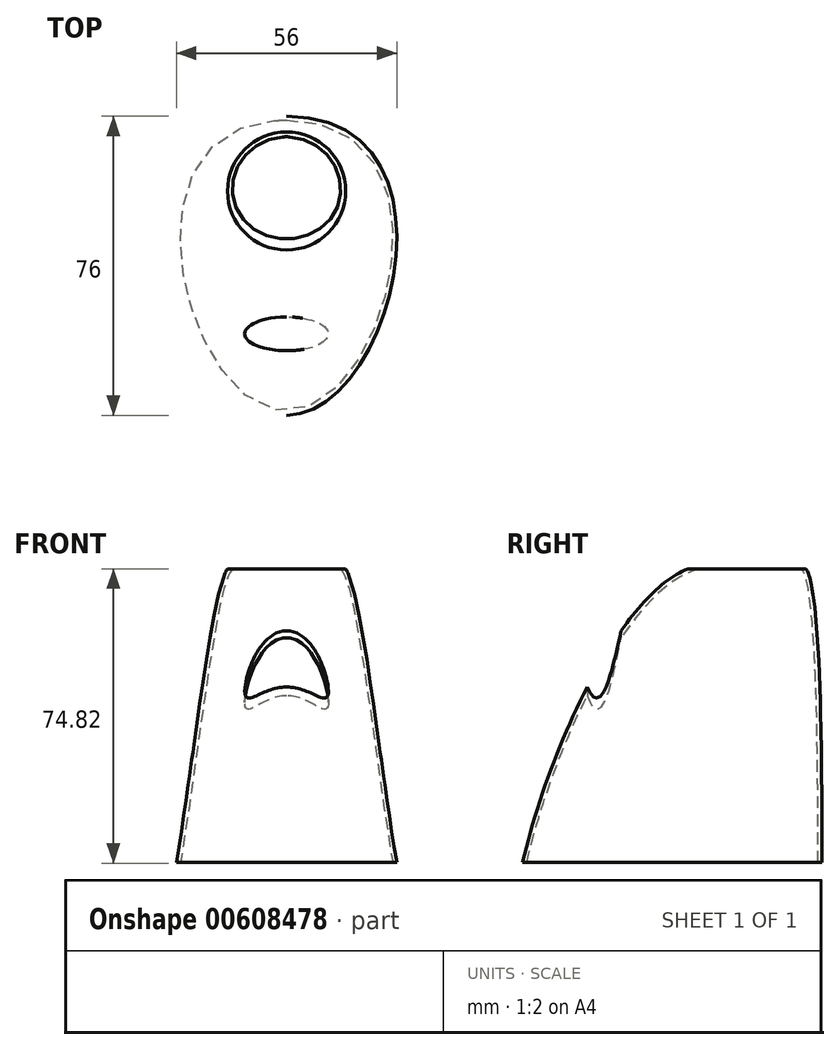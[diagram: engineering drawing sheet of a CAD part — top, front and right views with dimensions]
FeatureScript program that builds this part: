
annotation { "Feature Type Name" : "Feature", "Feature Type Description" : "" }
export const myFeature = defineFeature(function(context is Context, id is Id, definition is map)
    precondition{}
    {
        {
            var Q0;
            Q0=qCreatedBy(makeId("Top.planeOp"),FACE);
            var sketch = newSketch(context, id + "F0", { "sketchPlane" : qUnion([Q0])});
            skLineSegment(sketch, "E0", {"start": v(0, 0) * mm, "end": v(0, 38) * mm, "construction": true});
            skLineSegment(sketch, "E1", {"start": v(0, 0) * mm, "end": v(0, -38) * mm, "construction": true});
            skFitSpline(sketch, "E2", {"points": [v(0, 38) * mm, v(0, -38) * mm], "startDerivative": vector(139.24, 0) * mm, "endDerivative": vector(-81.05, 0) * mm});
            skLineSegment(sketch, "E3", {"start": v(28, 48.42) * mm, "end": v(28, -48.42) * mm, "construction": true});
            skFitSpline(sketch, "E4.MirrorCS", {"points": [v(0, 38) * mm, v(0, -38) * mm], "startDerivative": vector(-139.24, 0) * mm, "endDerivative": vector(81.05, 0) * mm});
            skSolve(sketch);
        }
        {
            var Q0;
            Q0=qCreatedBy(makeId("Top.planeOp"),FACE);
            cPlane(context, id + "F1", {"entities" : qUnion([Q0]), "cplaneType" : CPlaneType.OFFSET, "offset" : 74.6 * mm, "width" : 150 * mm, "height" : 150 * mm});
        }
        {
            var Q0;
            Q0=qCreatedBy(id+"F1.planeOp",FACE);
            var sketch = newSketch(context, id + "F2", { "sketchPlane" : qUnion([Q0])});
            skCircle(sketch, "E5", {"center": v(0, 19) * mm, "radius": 15 * mm});
            skPoint(sketch, "E6", {"position": v(0, 34) * mm});
            skPoint(sketch, "E7", {"position": v(0, 4) * mm});
            skSolve(sketch);
        }
        {
            var Q0;
            Q0=qCreatedBy(makeId("Right.planeOp"),FACE);
            var sketch = newSketch(context, id + "F3", { "sketchPlane" : qUnion([Q0])});
            skPoint(sketch, "E8.0", {"position": v(-38, 0) * mm});
            skPoint(sketch, "E9.0", {"position": v(4, 74.6) * mm});
            skFitSpline(sketch, "E10", {"points": [v(4, 74.6) * mm, v(-38, 0) * mm], "startDerivative": vector(-50.48, -19.63) * mm, "endDerivative": vector(-20.84, -91.06) * mm});
            skSolve(sketch);
        }
        {
            var Q0;
            Q0=qCreatedBy(makeId("Right.planeOp"),FACE);
            var sketch = newSketch(context, id + "F4", { "sketchPlane" : qUnion([Q0])});
            skPoint(sketch, "E11.0", {"position": v(34, 74.6) * mm});
            skPoint(sketch, "E12.0", {"position": v(38, 0) * mm});
            skLineSegment(sketch, "E13", {"start": v(38, 0) * mm, "end": v(38, 52.35) * mm, "construction": true});
            skFitSpline(sketch, "E14", {"points": [v(38, 0) * mm, v(34, 74.6) * mm], "startDerivative": vector(0, 67.18) * mm, "endDerivative": vector(-12, 16.6) * mm});
            skSolve(sketch);
        }
        {
            var Q0;
            Q0=makeQuery(id+"F0.imprint","IMPRINT",FACE,{"disambiguationData":[TD([[makeQuery(id+"F0.imprint","IMPRINT",EDGE,{"derivedFrom":sQuery(id+"F0.wireOp",EDGE,"E2")}),-1.0]])]});
            var Q1;
            Q1=makeQuery(id+"F2.imprint","IMPRINT",FACE,{"disambiguationData":[TD([[makeQuery(id+"F2.imprint","IMPRINT",EDGE,{"derivedFrom":sQuery(id+"F2.wireOp",EDGE,"E5")}),1.0]])]});
            var Q2;
            Q2=sQuery(id+"F3.wireOp",EDGE,"E10");
            var Q3;
            Q3=sQuery(id+"F4.wireOp",EDGE,"E14");
            loft(context, id + "F5", {"addGuides" : true, "sheetProfilesArray" : [{ "sheetProfileEntities" : qUnion([Q0]) }, { "sheetProfileEntities" : qUnion([Q1]) }], "guidesArray" : [{ "guideEntities" : qUnion([Q2]), "guideDerivativeType" : LoftGuideDerivativeType.DEFAULT, "guideDerivativeMagnitude" : 1 }, { "guideEntities" : qUnion([Q3]), "guideDerivativeType" : LoftGuideDerivativeType.DEFAULT, "guideDerivativeMagnitude" : 1 }]});
        }
        {
            var Q0;
            Q0=makeQuery(id+"F5.opLoft","CAP_FACE",FACE,{"disambiguationData":[OSD([makeQuery(id+"F2.imprint","IMPRINT",FACE,{"disambiguationData":[TD([[makeQuery(id+"F2.imprint","IMPRINT",EDGE,{"derivedFrom":sQuery(id+"F2.wireOp",EDGE,"E5")}),1.0]])]})])],"isStart":true});
            var Q1;
            Q1=makeQuery(id+"F5.opLoft","CAP_FACE",FACE,{"disambiguationData":[OSD([makeQuery(id+"F0.imprint","IMPRINT",FACE,{"disambiguationData":[TD([[makeQuery(id+"F0.imprint","IMPRINT",EDGE,{"derivedFrom":sQuery(id+"F0.wireOp",EDGE,"E2")}),-1.0]])]})])],"isStart":true});
            shell(context, id + "F6", {"entities" : qUnion([Q0, Q1]), "thickness" : 1 * mm});
        }
        {
            var Q0;
            Q0=qCreatedBy(makeId("Top.planeOp"),FACE);
            var sketch = newSketch(context, id + "F7", { "sketchPlane" : qUnion([Q0])});
            skEllipse(sketch, "E15", {"center": v(0, -17.3) * mm, "majorRadius": 10.63 * mm, "minorRadius": 4.3 * mm, "majorAxis": v(1, 0)});
            skSolve(sketch);
        }
        {
            var Q0;
            Q0 = qSketchRegion(id + "F7", true);
            extrude(context, id + "F8", {"entities" : qUnion([Q0]), "operationType" : NewBodyOperationType.REMOVE, "endBound" : BoundingType.THROUGH_ALL, "depth" : 25 * mm, "offsetDistance" : 25 * mm});
        }
    });
